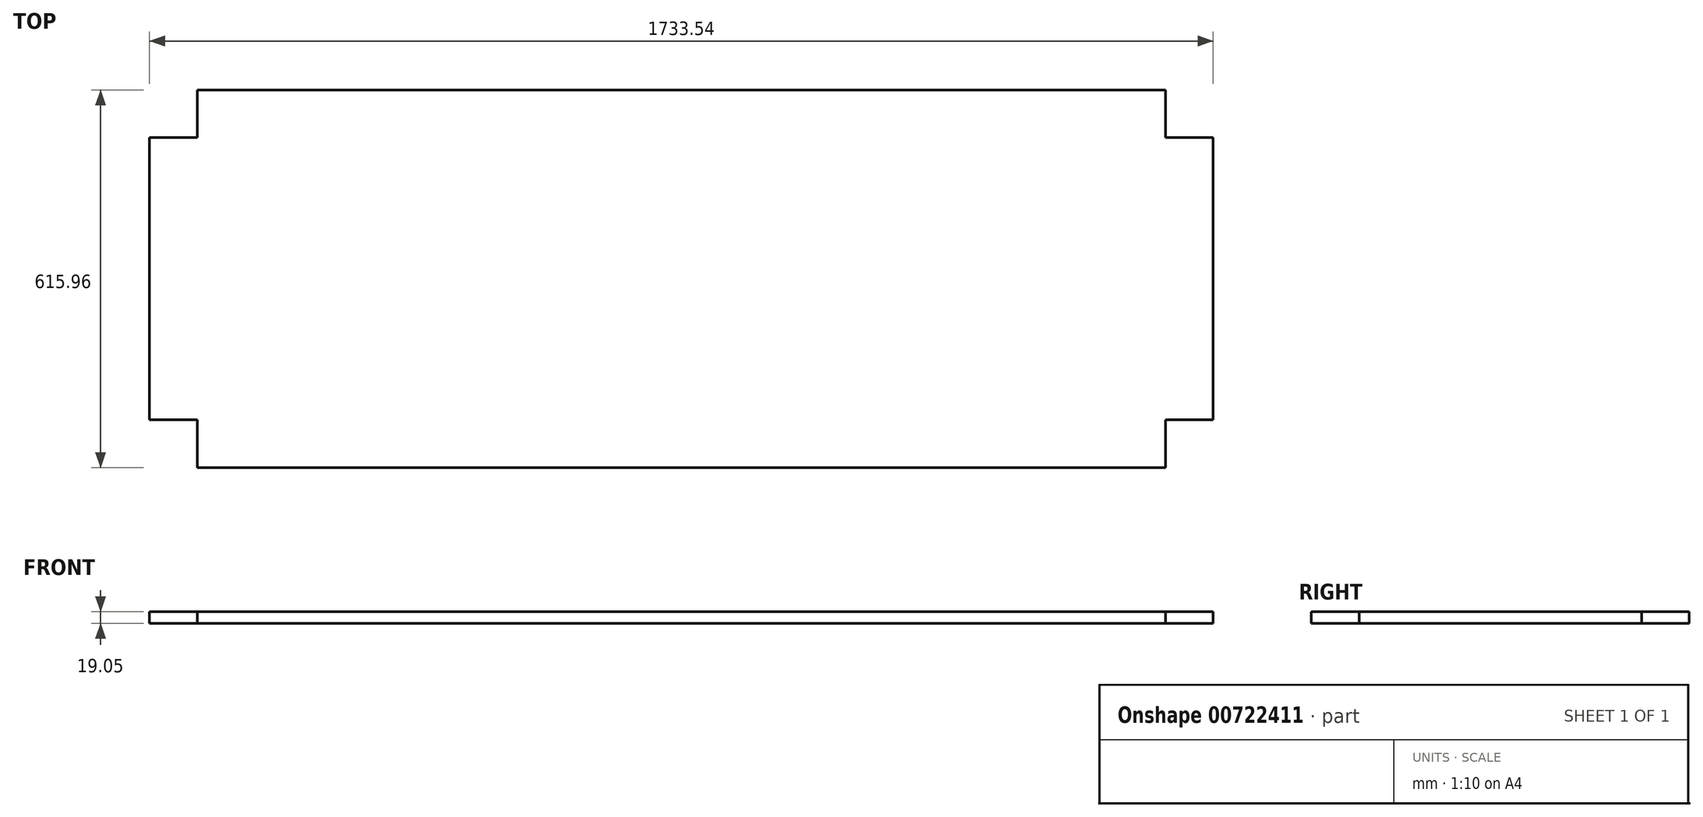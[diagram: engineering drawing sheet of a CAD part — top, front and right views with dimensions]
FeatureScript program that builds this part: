
annotation { "Feature Type Name" : "Feature", "Feature Type Description" : "" }
export const myFeature = defineFeature(function(context is Context, id is Id, definition is map)
    precondition{}
    {
        {
            var Q0;
            Q0=qCreatedBy(makeId("Top.planeOp"),FACE);
            var sketch = newSketch(context, id + "F0", { "sketchPlane" : qUnion([Q0])});
            skLineSegment(sketch, "E0.bottom", {"start": v(866.78, -307.98) * mm, "end": v(-866.78, -307.98) * mm});
            skLineSegment(sketch, "E0.top", {"start": v(866.78, 307.98) * mm, "end": v(-866.78, 307.98) * mm});
            skLineSegment(sketch, "E0.left", {"start": v(866.78, -307.98) * mm, "end": v(866.77, 307.98) * mm});
            skLineSegment(sketch, "E0.right", {"start": v(-866.78, -307.98) * mm, "end": v(-866.78, 307.98) * mm});
            skPoint(sketch, "E0.middle", {"position": v(0, 0) * mm});
            skLineSegment(sketch, "E1.bottom", {"start": v(-866.78, 307.98) * mm, "end": v(-788.99, 307.98) * mm});
            skLineSegment(sketch, "E1.top", {"start": v(-866.78, 230.19) * mm, "end": v(-788.99, 230.19) * mm});
            skLineSegment(sketch, "E1.left", {"start": v(-866.78, 307.98) * mm, "end": v(-866.78, 230.19) * mm});
            skLineSegment(sketch, "E1.right", {"start": v(-788.99, 307.97) * mm, "end": v(-788.99, 230.19) * mm});
            skLineSegment(sketch, "E2.bottom", {"start": v(-866.78, -307.98) * mm, "end": v(-788.99, -307.98) * mm});
            skLineSegment(sketch, "E2.top", {"start": v(-866.77, -230.19) * mm, "end": v(-788.99, -230.19) * mm});
            skLineSegment(sketch, "E2.left", {"start": v(-866.78, -307.98) * mm, "end": v(-866.78, -230.19) * mm});
            skLineSegment(sketch, "E2.right", {"start": v(-788.99, -307.98) * mm, "end": v(-788.99, -230.19) * mm});
            skLineSegment(sketch, "E3.bottom", {"start": v(866.78, -307.98) * mm, "end": v(788.99, -307.98) * mm});
            skLineSegment(sketch, "E3.top", {"start": v(866.78, -230.19) * mm, "end": v(788.99, -230.19) * mm});
            skLineSegment(sketch, "E3.left", {"start": v(866.78, -307.98) * mm, "end": v(866.78, -230.19) * mm});
            skLineSegment(sketch, "E3.right", {"start": v(788.99, -307.98) * mm, "end": v(788.99, -230.19) * mm});
            skLineSegment(sketch, "E4.bottom", {"start": v(866.78, 307.98) * mm, "end": v(788.99, 307.98) * mm});
            skLineSegment(sketch, "E4.top", {"start": v(866.78, 230.19) * mm, "end": v(788.99, 230.19) * mm});
            skLineSegment(sketch, "E4.left", {"start": v(866.78, 307.98) * mm, "end": v(866.78, 230.19) * mm});
            skLineSegment(sketch, "E4.right", {"start": v(788.99, 307.98) * mm, "end": v(788.99, 230.19) * mm});
            skSolve(sketch);
        }
        {
            var Q0;
            {var subQ3=sQuery(id+"F0.wireOp",EDGE,"E1.top");Q0=makeQuery(id+"F0.imprint","IMPRINT",FACE,{"disambiguationData":[TD([[makeQuery(id+"F0.imprint","IMPRINT",EDGE,{"derivedFrom":subQ3}),-1.0]])]});}
            extrude(context, id + "F1", {"entities" : qUnion([Q0]), "depth" : 19.05 * mm, "offsetDistance" : 25.4 * mm});
        }
    });
